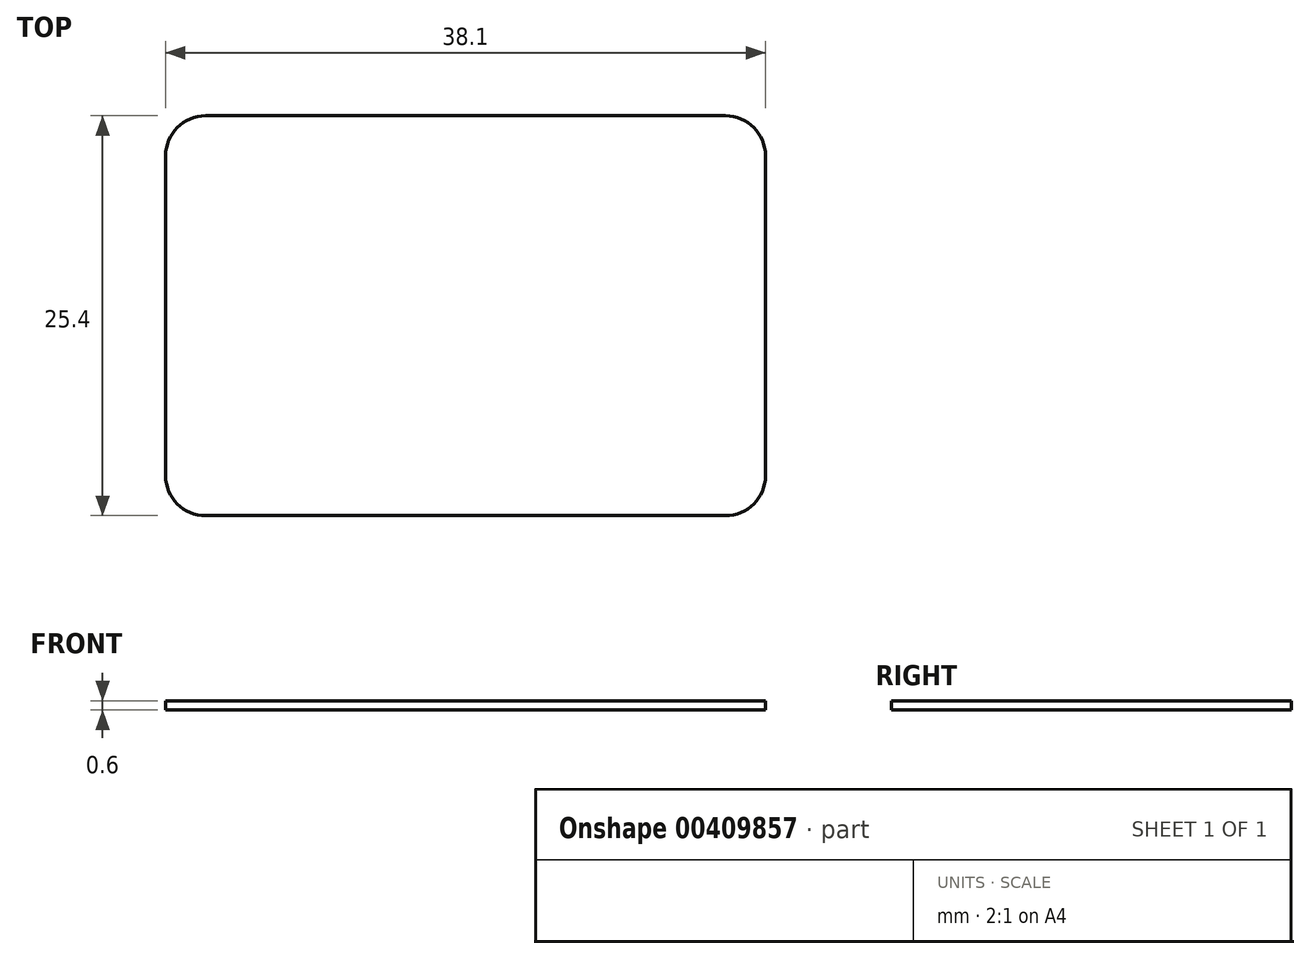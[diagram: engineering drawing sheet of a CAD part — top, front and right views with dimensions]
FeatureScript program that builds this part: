
annotation { "Feature Type Name" : "Feature", "Feature Type Description" : "" }
export const myFeature = defineFeature(function(context is Context, id is Id, definition is map)
    precondition{}
    {
        {
            var Q0;
            Q0=qCreatedBy(makeId("Top.planeOp"),FACE);
            var sketch = newSketch(context, id + "F0", { "sketchPlane" : qUnion([Q0])});
            skLineSegment(sketch, "E0.bottom", {"start": v(19.05, 12.7) * mm, "end": v(-19.05, 12.7) * mm});
            skLineSegment(sketch, "E0.top", {"start": v(19.05, -12.7) * mm, "end": v(-19.05, -12.7) * mm});
            skLineSegment(sketch, "E0.left", {"start": v(19.05, 12.7) * mm, "end": v(19.05, -12.7) * mm});
            skLineSegment(sketch, "E0.right", {"start": v(-19.05, 12.7) * mm, "end": v(-19.05, -12.7) * mm});
            skPoint(sketch, "E0.middle", {"position": v(0, 0) * mm});
            skSolve(sketch);
        }
        {
            var Q0;
            Q0 = qSketchRegion(id + "F0", true);
            extrude(context, id + "F1", {"entities" : qUnion([Q0]), "depth" : .6 * mm});
        }
        {
            var Q0;
            Q0=makeQuery(id+"F1.opExtrude","SWEPT_EDGE",EDGE,{"disambiguationData":[OSD([sQuery(id+"F0.wireOp",EDGE,"E0.top"),sQuery(id+"F0.wireOp",EDGE,"E0.left")])]});
            var Q1;
            Q1=makeQuery(id+"F1.opExtrude","SWEPT_EDGE",EDGE,{"disambiguationData":[OSD([sQuery(id+"F0.wireOp",EDGE,"E0.top"),sQuery(id+"F0.wireOp",EDGE,"E0.right")])]});
            var Q2;
            Q2=makeQuery(id+"F1.opExtrude","SWEPT_EDGE",EDGE,{"disambiguationData":[OSD([sQuery(id+"F0.wireOp",EDGE,"E0.bottom"),sQuery(id+"F0.wireOp",EDGE,"E0.right")])]});
            var Q3;
            Q3=makeQuery(id+"F1.opExtrude","SWEPT_EDGE",EDGE,{"disambiguationData":[OSD([sQuery(id+"F0.wireOp",EDGE,"E0.bottom"),sQuery(id+"F0.wireOp",EDGE,"E0.left")])]});
            fillet(context, id + "F2", {"entities" : qUnion([Q0, Q1, Q2, Q3]), "radius" : 2.54 * mm, "tangentPropagation" : true, "allowEdgeOverflow" : false});
        }
    });
